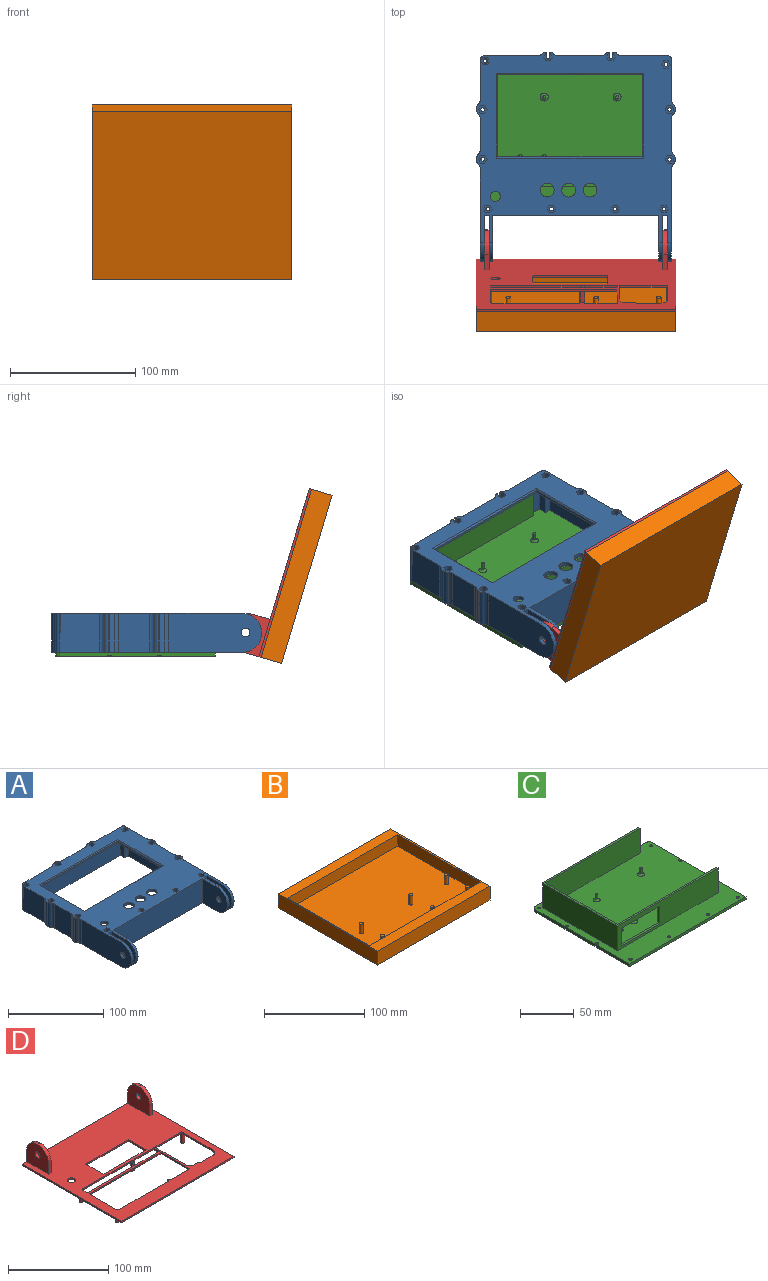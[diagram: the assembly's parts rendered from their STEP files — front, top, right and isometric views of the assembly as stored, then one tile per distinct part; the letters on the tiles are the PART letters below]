
ASSEMBLY  parts=4 mates=3
PART A: 191 faces, bbox 158.4x167x31 mm
  f0: plane 140.4x112mm, normal (0,0,-1), area 7821.9mm2, adj f2,f26,f29,f30,f31,f32,f33,f36
  f1: plane 158.4x152mm, normal (0,0,1), area 11149.3mm2, adj f9,f10,f17,f18,f19,f20,f21,f22
  f2: plane 105x28mm, normal (-1,0,0), area 2939.8mm2, adj f0,f24,f36,f56,f81,f82,f87,f88
  f3: cylinder r=1.5mm len=16mm, axis (0,0,-1), area 150.8mm2, adj f24,f166
  f4: cylinder r=1.5mm len=16mm, axis (0,0,-1), area 150.8mm2, adj f24,f159
  f5: cylinder r=1.5mm len=16mm, axis (0,0,-1), area 150.8mm2, adj f24,f152
  f6: cylinder r=1.5mm len=16mm, axis (0,0,-1), area 150.8mm2, adj f24,f145
  f7: cylinder r=1.5mm len=16mm, axis (0,0,-1), area 110.4mm2, adj f10,f24,f71,f130
  f8: cylinder r=1.5mm len=16mm, axis (0,0,-1), area 110.4mm2, adj f9,f24,f68,f138
  f9: plane 31x3mm, normal (1,0,0), area 62.5mm2, adj f1,f8,f24,f67,f133,f138
  f10: plane 31x3mm, normal (1,0,0), area 62.5mm2, adj f1,f7,f24,f70,f125,f130
  f11: cylinder r=1.5mm len=16mm, axis (0,0,-1), area 150.8mm2, adj f24,f122
  f12: cylinder r=1.75mm len=16mm, axis (0,0,-1), area 175.9mm2, adj f24,f115
  f13: cylinder r=1.5mm len=16mm, axis (0,0,-1), area 150.8mm2, adj f24,f108
  f14: cylinder r=1.5mm len=16mm, axis (0,0,-1), area 150.8mm2, adj f24,f101
  f15: cylinder r=1.5mm len=16mm, axis (0,0,-1), area 150.8mm2, adj f24,f94
  f16: cylinder r=1.5mm len=16mm, axis (0,0,-1), area 150.8mm2, adj f24,f87
  f17: plane 31x24.88mm, normal (1,0,0), area 771.4mm2, adj f1,f24,f175,f178
  f18: plane 73.94x31mm, normal (1,0,0), area 2157.1mm2, adj f1,f24,f43,f44,f45,f62,f177
  f19: plane 31x24.88mm, normal (-1,0,0), area 771.4mm2, adj f1,f24,f179,f182
  f20: plane 31.94x31mm, normal (-1,0,0), area 990.2mm2, adj f1,f24,f51,f181
  f21: plane 34.01x31mm, normal (0,1,0), area 1054.3mm2, adj f1,f24,f187,f190
  f22: plane 36.76x31mm, normal (0,1,0), area 1139.4mm2, adj f1,f24,f50,f189
  f23: plane 42.66x31mm, normal (0,1,0), area 1322.3mm2, adj f1,f24,f51,f188
  f24: plane 158.4x152mm, normal (0,0,-1), area 3979.4mm2, adj f2,f3,f4,f5,f6,f7,f8,f9
  f25: plane 31x4mm, normal (0,-1,0), area 124mm2, adj f1,f24,f42,f58
  f26: plane 135.4x28mm, normal (0,-1,0), area 3791.2mm2, adj f0,f24,f33,f57
  f27: plane 132.4x31mm, normal (0,-1,0), area 4104.4mm2, adj f1,f24,f40,f59
  f28: plane 31x4mm, normal (0,-1,0), area 124mm2, adj f1,f24,f37,f39
  f29: plane 65.5x2mm, normal (1,0,0), area 131mm2, adj f0,f30,f32,f53
  f30: plane 115x2mm, normal (0,-1,0), area 230mm2, adj f0,f29,f31,f52
  f31: plane 65.5x2mm, normal (-1,0,0), area 131mm2, adj f0,f30,f32,f54
  f32: plane 115x2mm, normal (0,1,0), area 230mm2, adj f0,f29,f31,f55
  f33: plane 112x28mm, normal (1,0,0), area 3136mm2, adj f0,f24,f26,f36
  f34: plane 73.94x31mm, normal (-1,0,0), area 2157.1mm2, adj f1,f24,f38,f48,f49,f64,f180
  f35: plane 31.94x31mm, normal (1,0,0), area 990.2mm2, adj f1,f24,f50,f176
  f36: plane 140.4x28mm, normal (0,1,0), area 3931.2mm2, adj f0,f2,f24,f33
  f37: plane 37x31mm, normal (1,0,0), area 1011.9mm2, adj f1,f24,f28,f38,f48,f49,f64
  f38: plane 3x1mm, normal (0,-1,0), area 3mm2, adj f34,f37,f48,f49
  f39: plane 37x31mm, normal (-1,0,0), area 1011.9mm2, adj f1,f24,f28,f41,f46,f47,f63
  f40: plane 37x31mm, normal (1,0,0), area 1011.9mm2, adj f1,f24,f27,f41,f46,f47,f63
  f41: plane 3x1mm, normal (0,-1,0), area 3mm2, adj f39,f40,f46,f47
  f42: plane 37x31mm, normal (-1,0,0), area 1011.9mm2, adj f1,f24,f25,f43,f44,f45,f62
  f43: plane 3x1mm, normal (0,-1,0), area 3mm2, adj f18,f42,f44,f45
  f44: cylinder r=15mm len=15mm, axis (-1,0,0), area 70.7mm2, adj f18,f24,f42,f43
  f45: cylinder r=15mm len=15mm, axis (1,0,0), area 70.7mm2, adj f1,f18,f42,f43
  f46: cylinder r=15mm len=15mm, axis (-1,0,0), area 70.7mm2, adj f24,f39,f40,f41
  f47: cylinder r=15mm len=15mm, axis (1,0,0), area 70.7mm2, adj f1,f39,f40,f41
  f48: cylinder r=15mm len=15mm, axis (1,0,0), area 70.7mm2, adj f1,f34,f37,f38
  f49: cylinder r=15mm len=15mm, axis (-1,0,0), area 70.7mm2, adj f24,f34,f37,f38
  f50: cylinder r=3mm len=31mm, axis (0,0,1), area 146.1mm2, adj f1,f22,f24,f35
  f51: cylinder r=3mm len=31mm, axis (0,0,-1), area 146.1mm2, adj f1,f20,f23,f24
  f52: plane 117x1mm, normal (0,-0.71,0.71), area 164mm2, adj f1,f30,f53,f54
  f53: plane 67.5x1mm, normal (0.71,0,0.71), area 94mm2, adj f1,f29,f52,f55
  f54: plane 67.5x1mm, normal (-0.71,0,0.71), area 94mm2, adj f1,f31,f52,f55
  f55: plane 117x1mm, normal (0,0.71,0.71), area 164mm2, adj f1,f32,f53,f54
  f56: plane 28x5mm, normal (0,-1,0), area 140mm2, adj f0,f2,f24,f57
  f57: plane 28x7mm, normal (-1,0,0), area 196mm2, adj f0,f24,f26,f56
  f58: plane 37x31mm, normal (1,0,0), area 1011.9mm2, adj f1,f24,f25,f60,f61,f65,f66
  f59: plane 37x31mm, normal (-1,0,0), area 1011.9mm2, adj f1,f24,f27,f60,f61,f65,f66
  f60: plane 3x1mm, normal (0,-1,0), area 3mm2, adj f58,f59,f65,f66
  f61: cylinder r=3.5mm len=7mm, axis (-1,0,0), area 66mm2, adj f58,f59
  f62: cylinder r=3.5mm len=7mm, axis (-1,0,0), area 66mm2, adj f18,f42
  f63: cylinder r=3.5mm len=7mm, axis (-1,0,0), area 66mm2, adj f39,f40
  f64: cylinder r=3.5mm len=7mm, axis (-1,0,0), area 66mm2, adj f34,f37
  f65: cylinder r=15mm len=15mm, axis (1,0,0), area 70.7mm2, adj f1,f58,f59,f60
  f66: cylinder r=15mm len=15mm, axis (-1,0,0), area 70.7mm2, adj f24,f58,f59,f60
  f67: plane 31x0.58mm, normal (0,1,0), area 18mm2, adj f1,f9,f24,f186
  f68: plane 31x3mm, normal (-1,0,0), area 62.5mm2, adj f1,f8,f24,f69,f132,f138
  f69: plane 31x1.18mm, normal (0,1,0), area 36.6mm2, adj f1,f24,f68,f185
  f70: plane 31x0.98mm, normal (0,1,0), area 30.4mm2, adj f1,f10,f24,f184
  f71: plane 31x3mm, normal (-1,0,0), area 62.5mm2, adj f1,f7,f24,f72,f124,f130
  f72: plane 31x0.78mm, normal (0,1,0), area 24.2mm2, adj f1,f24,f71,f183
  f73: cylinder r=5.5mm len=11mm, axis (0,0,-1), area 103.7mm2, adj f0,f1
  f74: cylinder r=5.5mm len=11mm, axis (0,0,-1), area 103.7mm2, adj f0,f1
  f75: cylinder r=5.5mm len=11mm, axis (0,0,-1), area 103.7mm2, adj f0,f1
  f76: cylinder r=4mm len=8mm, axis (0,0,-1), area 75.4mm2, adj f0,f1
  f77: plane 31x0.84mm, normal (-1,0,0), area 25.9mm2, adj f1,f24,f171,f172
  f78: plane 31x0.84mm, normal (-1,0,0), area 25.9mm2, adj f1,f24,f173,f174
  f79: plane 31x0.84mm, normal (1,0,0), area 25.9mm2, adj f1,f24,f169,f170
  f80: plane 31x0.84mm, normal (1,0,0), area 25.9mm2, adj f1,f24,f167,f168
  f81: plane 15x3.03mm, normal (0.87,0.5,0), area 52.5mm2, adj f0,f1,f2,f82,f83,f87
  f82: plane 15x3.03mm, normal (0.87,-0.5,0), area 52.5mm2, adj f0,f1,f2,f81,f86,f87
  f83: plane 15x3.5mm, normal (0,1,0), area 52.5mm2, adj f1,f81,f84,f87
  f84: plane 15x3.03mm, normal (-0.87,0.5,0), area 52.5mm2, adj f1,f83,f85,f87
  f85: plane 15x3.03mm, normal (-0.87,-0.5,0), area 52.5mm2, adj f1,f84,f86,f87
  f86: plane 15x3.5mm, normal (0,-1,0), area 52.5mm2, adj f1,f82,f85,f87
  f87: plane 7x6.06mm, normal (0,0,1), area 24.8mm2, adj f2,f16,f81,f82,f83,f84,f85,f86
  f88: plane 15x3.03mm, normal (0.87,0.5,0), area 52.5mm2, adj f0,f1,f2,f89,f90,f94
  f89: plane 15x3.03mm, normal (0.87,-0.5,0), area 52.5mm2, adj f0,f1,f2,f88,f93,f94
  f90: plane 15x3.5mm, normal (0,1,0), area 52.5mm2, adj f1,f88,f91,f94
  f91: plane 15x3.03mm, normal (-0.87,0.5,0), area 52.5mm2, adj f1,f90,f92,f94
  f92: plane 15x3.03mm, normal (-0.87,-0.5,0), area 52.5mm2, adj f1,f91,f93,f94
  f93: plane 15x3.5mm, normal (0,-1,0), area 52.5mm2, adj f1,f89,f92,f94
  f94: plane 7x6.06mm, normal (0,0,1), area 24.8mm2, adj f2,f15,f88,f89,f90,f91,f92,f93
  f95: plane 15x3.03mm, normal (0.87,0.5,0), area 52.5mm2, adj f1,f96,f100,f101
  f96: plane 15x3.5mm, normal (0,1,0), area 52.5mm2, adj f1,f95,f97,f101
  f97: plane 15x3.03mm, normal (-0.87,0.5,0), area 52.5mm2, adj f1,f96,f98,f101
  f98: plane 15x3.03mm, normal (-0.87,-0.5,0), area 52.5mm2, adj f1,f97,f99,f101
  f99: plane 15x3.5mm, normal (0,-1,0), area 52.5mm2, adj f1,f98,f100,f101
  f100: plane 15x3.03mm, normal (0.87,-0.5,0), area 52.5mm2, adj f1,f95,f99,f101
  f101: plane 7x6.06mm, normal (0,0,1), area 24.8mm2, adj f14,f95,f96,f97,f98,f99,f100
  f102: plane 15x3.03mm, normal (0.87,0.5,0), area 52.5mm2, adj f1,f103,f107,f108
  f103: plane 15x3.5mm, normal (0,1,0), area 52.5mm2, adj f1,f102,f104,f108
  f104: plane 15x3.03mm, normal (-0.87,0.5,0), area 52.5mm2, adj f1,f103,f105,f108
  f105: plane 15x3.03mm, normal (-0.87,-0.5,0), area 52.5mm2, adj f1,f104,f106,f108
  f106: plane 15x3.5mm, normal (0,-1,0), area 52.5mm2, adj f1,f105,f107,f108
  f107: plane 15x3.03mm, normal (0.87,-0.5,0), area 52.5mm2, adj f1,f102,f106,f108
  f108: plane 7x6.06mm, normal (0,0,1), area 24.8mm2, adj f13,f102,f103,f104,f105,f106,f107
  f109: plane 15x3.03mm, normal (0.87,0.5,0), area 52.5mm2, adj f1,f110,f114,f115
  f110: plane 15x3.5mm, normal (0,1,0), area 52.5mm2, adj f1,f109,f111,f115
  f111: plane 15x3.03mm, normal (-0.87,0.5,0), area 52.5mm2, adj f1,f110,f112,f115
  f112: plane 15x3.03mm, normal (-0.87,-0.5,0), area 52.5mm2, adj f1,f111,f113,f115
  f113: plane 15x3.5mm, normal (0,-1,0), area 52.5mm2, adj f1,f112,f114,f115
  f114: plane 15x3.03mm, normal (0.87,-0.5,0), area 52.5mm2, adj f1,f109,f113,f115
  f115: plane 7x6.06mm, normal (0,0,1), area 22.2mm2, adj f12,f109,f110,f111,f112,f113,f114
  f116: plane 15x3.03mm, normal (0.87,0.5,0), area 52.5mm2, adj f1,f117,f121,f122
  f117: plane 15x3.5mm, normal (0,1,0), area 52.5mm2, adj f1,f116,f118,f122
  f118: plane 15x3.03mm, normal (-0.87,0.5,0), area 52.5mm2, adj f1,f117,f119,f122
  f119: plane 15x3.03mm, normal (-0.87,-0.5,0), area 52.5mm2, adj f1,f118,f120,f122
  f120: plane 15x3.5mm, normal (0,-1,0), area 52.5mm2, adj f1,f119,f121,f122
  f121: plane 15x3.03mm, normal (0.87,-0.5,0), area 52.5mm2, adj f1,f116,f120,f122
  f122: plane 7x6.06mm, normal (0,0,1), area 24.8mm2, adj f11,f116,f117,f118,f119,f120,f121
  f123: plane 15x3.03mm, normal (-0.87,-0.5,0), area 52.5mm2, adj f1,f124,f129,f130
  f124: plane 15x0.63mm, normal (0,-1,0), area 9.5mm2, adj f1,f71,f123,f130
  f125: plane 15x0.63mm, normal (0,-1,0), area 9.5mm2, adj f1,f10,f126,f130
  f126: plane 15x3.03mm, normal (0.87,-0.5,0), area 52.5mm2, adj f1,f125,f127,f130
  f127: plane 15x3.03mm, normal (0.87,0.5,0), area 52.5mm2, adj f1,f126,f128,f130
  f128: plane 15x3.5mm, normal (0,1,0), area 52.5mm2, adj f1,f127,f129,f130
  f129: plane 15x3.03mm, normal (-0.87,0.5,0), area 52.5mm2, adj f1,f123,f128,f130
  f130: plane 7x6.06mm, normal (0,0,1), area 21mm2, adj f7,f10,f71,f123,f124,f125,f126,f127
  f131: plane 15x3.03mm, normal (-0.87,-0.5,0), area 52.5mm2, adj f1,f132,f137,f138
  f132: plane 15x0.63mm, normal (0,-1,0), area 9.5mm2, adj f1,f68,f131,f138
  f133: plane 15x0.63mm, normal (0,-1,0), area 9.5mm2, adj f1,f9,f134,f138
  f134: plane 15x3.03mm, normal (0.87,-0.5,0), area 52.5mm2, adj f1,f133,f135,f138
  f135: plane 15x3.03mm, normal (0.87,0.5,0), area 52.5mm2, adj f1,f134,f136,f138
  f136: plane 15x3.5mm, normal (0,1,0), area 52.5mm2, adj f1,f135,f137,f138
  f137: plane 15x3.03mm, normal (-0.87,0.5,0), area 52.5mm2, adj f1,f131,f136,f138
  f138: plane 7x6.06mm, normal (0,0,1), area 21mm2, adj f8,f9,f68,f131,f132,f133,f134,f135
  f139: plane 15x3.03mm, normal (0.87,0.5,0), area 52.5mm2, adj f1,f140,f144,f145
  f140: plane 15x3.5mm, normal (0,1,0), area 52.5mm2, adj f1,f139,f141,f145
  f141: plane 15x3.03mm, normal (-0.87,0.5,0), area 52.5mm2, adj f1,f140,f142,f145
  f142: plane 15x3.03mm, normal (-0.87,-0.5,0), area 52.5mm2, adj f1,f141,f143,f145
  f143: plane 15x3.5mm, normal (0,-1,0), area 52.5mm2, adj f1,f142,f144,f145
  f144: plane 15x3.03mm, normal (0.87,-0.5,0), area 52.5mm2, adj f1,f139,f143,f145
  f145: plane 7x6.06mm, normal (0,0,1), area 24.8mm2, adj f6,f139,f140,f141,f142,f143,f144
  f146: plane 15x3.03mm, normal (0.87,0.5,0), area 52.5mm2, adj f1,f147,f151,f152
  f147: plane 15x3.5mm, normal (0,1,0), area 52.5mm2, adj f1,f146,f148,f152
  f148: plane 15x3.03mm, normal (-0.87,0.5,0), area 52.5mm2, adj f1,f147,f149,f152
  f149: plane 15x3.03mm, normal (-0.87,-0.5,0), area 52.5mm2, adj f1,f148,f150,f152
  f150: plane 15x3.5mm, normal (0,-1,0), area 52.5mm2, adj f1,f149,f151,f152
  f151: plane 15x3.03mm, normal (0.87,-0.5,0), area 52.5mm2, adj f1,f146,f150,f152
  f152: plane 7x6.06mm, normal (0,0,1), area 24.8mm2, adj f5,f146,f147,f148,f149,f150,f151
  f153: plane 15x3.03mm, normal (0.87,0.5,0), area 52.5mm2, adj f1,f154,f158,f159
  f154: plane 15x3.5mm, normal (0,1,0), area 52.5mm2, adj f1,f153,f155,f159
  f155: plane 15x3.03mm, normal (-0.87,0.5,0), area 52.5mm2, adj f1,f154,f156,f159
  f156: plane 15x3.03mm, normal (-0.87,-0.5,0), area 52.5mm2, adj f1,f155,f157,f159
  f157: plane 15x3.5mm, normal (0,-1,0), area 52.5mm2, adj f1,f156,f158,f159
  f158: plane 15x3.03mm, normal (0.87,-0.5,0), area 52.5mm2, adj f1,f153,f157,f159
  f159: plane 7x6.06mm, normal (0,0,1), area 24.8mm2, adj f4,f153,f154,f155,f156,f157,f158
  f160: plane 15x3.03mm, normal (0.87,0.5,0), area 52.5mm2, adj f1,f161,f165,f166
  f161: plane 15x3.5mm, normal (0,1,0), area 52.5mm2, adj f1,f160,f162,f166
  f162: plane 15x3.03mm, normal (-0.87,0.5,0), area 52.5mm2, adj f1,f161,f163,f166
  f163: plane 15x3.03mm, normal (-0.87,-0.5,0), area 52.5mm2, adj f1,f162,f164,f166
  f164: plane 15x3.5mm, normal (0,-1,0), area 52.5mm2, adj f1,f163,f165,f166
  f165: plane 15x3.03mm, normal (0.87,-0.5,0), area 52.5mm2, adj f1,f160,f164,f166
  f166: plane 7x6.06mm, normal (0,0,1), area 24.8mm2, adj f3,f160,f161,f162,f163,f164,f165
  f167: cylinder r=5mm len=31mm, axis (0,0,1), area 123.3mm2, adj f1,f24,f80,f175
  f168: cylinder r=5mm len=31mm, axis (0,0,1), area 123.3mm2, adj f1,f24,f80,f176
  f169: cylinder r=5mm len=31mm, axis (0,0,1), area 123.3mm2, adj f1,f24,f79,f177
  f170: cylinder r=5mm len=31mm, axis (0,0,1), area 123.3mm2, adj f1,f24,f79,f178
  f171: cylinder r=5mm len=31mm, axis (0,0,-1), area 123.3mm2, adj f1,f24,f77,f179
  f172: cylinder r=5mm len=31mm, axis (0,0,-1), area 123.3mm2, adj f1,f24,f77,f180
  f173: cylinder r=5mm len=31mm, axis (0,0,-1), area 123.3mm2, adj f1,f24,f78,f181
  f174: cylinder r=5mm len=31mm, axis (0,0,-1), area 123.3mm2, adj f1,f24,f78,f182
  f175: cylinder r=5mm len=31mm, axis (0,0,1), area 123.3mm2, adj f1,f17,f24,f167
  f176: cylinder r=5mm len=31mm, axis (0,0,1), area 123.3mm2, adj f1,f24,f35,f168
  f177: cylinder r=5mm len=31mm, axis (0,0,1), area 123.3mm2, adj f1,f18,f24,f169
  f178: cylinder r=5mm len=31mm, axis (0,0,1), area 123.3mm2, adj f1,f17,f24,f170
  f179: cylinder r=5mm len=31mm, axis (0,0,-1), area 123.3mm2, adj f1,f19,f24,f171
  f180: cylinder r=5mm len=31mm, axis (0,0,-1), area 123.3mm2, adj f1,f24,f34,f172
  f181: cylinder r=5mm len=31mm, axis (0,0,-1), area 123.3mm2, adj f1,f20,f24,f173
  f182: cylinder r=5mm len=31mm, axis (0,0,-1), area 123.3mm2, adj f1,f19,f24,f174
  f183: cylinder r=3mm len=31mm, axis (0,0,1), area 83.3mm2, adj f1,f24,f72,f187
  f184: cylinder r=3mm len=31mm, axis (0,0,-1), area 83.3mm2, adj f1,f24,f70,f188
  f185: cylinder r=3mm len=31mm, axis (0,0,1), area 83.3mm2, adj f1,f24,f69,f189
  f186: cylinder r=3mm len=31mm, axis (0,0,-1), area 83.3mm2, adj f1,f24,f67,f190
  f187: cylinder r=5mm len=31mm, axis (0,0,1), area 138.8mm2, adj f1,f21,f24,f183
  f188: cylinder r=5mm len=31mm, axis (0,0,-1), area 138.8mm2, adj f1,f23,f24,f184
  f189: cylinder r=5mm len=31mm, axis (0,0,1), area 138.8mm2, adj f1,f22,f24,f185
  f190: cylinder r=5mm len=31mm, axis (0,0,-1), area 138.8mm2, adj f1,f21,f24,f186
PART B: 23 faces, bbox 159x140x17 mm
  f0: plane 155.5x116mm, normal (0,0,1), area 17962.6mm2, adj f2,f3,f4,f5,f11,f13,f15,f17
  f1: plane 159x140mm, normal (0,0,-1), area 22260mm2, adj f6,f7,f8,f9
  f2: plane 155.5x14mm, normal (0,-1,0), area 2177mm2, adj f0,f3,f5,f10
  f3: plane 116x14mm, normal (1,0,0), area 1624mm2, adj f0,f2,f4,f10
  f4: plane 155.5x14mm, normal (0,1,0), area 2177mm2, adj f0,f3,f5,f10
  f5: plane 116x14mm, normal (-1,0,0), area 1624mm2, adj f0,f2,f4,f10
  f6: plane 159x17mm, normal (0,1,0), area 2703mm2, adj f1,f7,f9,f10
  f7: plane 140x17mm, normal (-1,0,0), area 2380mm2, adj f1,f6,f8,f10
  f8: plane 159x17mm, normal (0,-1,0), area 2703mm2, adj f1,f7,f9,f10
  f9: plane 140x17mm, normal (1,0,0), area 2380mm2, adj f1,f6,f8,f10
  f10: plane 159x140mm, normal (0,0,1), area 4222mm2, adj f2,f3,f4,f5,f6,f7,f8,f9
  f11: cylinder r=2mm len=11.4mm, axis (0,0,-1), area 143.3mm2, adj f0,f12
  f12: plane 4x4mm, normal (0,0,1), area 12.6mm2, adj f11
  f13: cylinder r=2mm len=11.4mm, axis (0,0,-1), area 143.3mm2, adj f0,f14
  f14: plane 4x4mm, normal (0,0,1), area 12.6mm2, adj f13
  f15: cylinder r=2mm len=11.4mm, axis (0,0,-1), area 143.3mm2, adj f0,f16
  f16: plane 4x4mm, normal (0,0,1), area 12.6mm2, adj f15
  f17: cylinder r=2mm len=11.4mm, axis (0,0,-1), area 143.3mm2, adj f0,f18
  f18: plane 4x4mm, normal (0,0,1), area 12.6mm2, adj f17
  f19: cylinder r=2mm len=11.4mm, axis (0,0,-1), area 143.3mm2, adj f0,f20
  f20: plane 4x4mm, normal (0,0,1), area 12.6mm2, adj f19
  f21: cylinder r=2mm len=11.4mm, axis (0,0,-1), area 143.3mm2, adj f0,f22
  f22: plane 4x4mm, normal (0,0,1), area 12.6mm2, adj f21
PART C: 71 faces, bbox 152.4x127x31 mm
  f0: plane 124x3mm, normal (1,0,0), area 366.3mm2, adj f17,f18,f19,f44,f63,f64,f65,f66
  f1: cylinder r=1.5mm len=3mm, axis (0,0,-1), area 18.8mm2, adj f18,f66
  f2: cylinder r=1.5mm len=3mm, axis (0,0,-1), area 18.8mm2, adj f18,f64
  f3: cylinder r=1.5mm len=3mm, axis (0,0,-1), area 18.8mm2, adj f18,f62
  f4: cylinder r=1.5mm len=3mm, axis (0,0,-1), area 18.8mm2, adj f18,f60
  f5: cylinder r=1.5mm len=3mm, axis (0,0,-1), area 18.8mm2, adj f18,f58
  f6: cylinder r=1.5mm len=3mm, axis (0,0,-1), area 18.8mm2, adj f18,f56
  f7: cylinder r=1.5mm len=3mm, axis (0,0,-1), area 18.8mm2, adj f18,f54
  f8: cylinder r=1.5mm len=3mm, axis (0,0,-1), area 18.8mm2, adj f18,f52
  f9: cylinder r=1.5mm len=3mm, axis (0,0,-1), area 18.8mm2, adj f18,f50
  f10: cylinder r=1.5mm len=3mm, axis (0,0,-1), area 18.8mm2, adj f18,f48
  f11: plane 44.18x3mm, normal (0,1,0), area 131.6mm2, adj f18,f19,f44,f46,f69,f70
  f12: plane 47.86x3mm, normal (0,1,0), area 141.8mm2, adj f18,f19,f45,f46,f67,f68,f69,f70
  f13: plane 129.94x28mm, normal (0,1,0), area 2638.4mm2, adj f18,f20,f22,f26,f35,f36,f37,f38
  f14: plane 131.94x28mm, normal (0,-1,0), area 2694.4mm2, adj f18,f20,f22,f23,f35,f36,f37,f38
  f15: plane 49.88x3mm, normal (0,1,0), area 148.7mm2, adj f18,f19,f43,f45,f67,f68
  f16: plane 124x3mm, normal (-1,0,0), area 367.9mm2, adj f17,f18,f19,f43,f49,f50,f51,f52
  f17: plane 152.4x3mm, normal (0,-1,0), area 457.2mm2, adj f0,f16,f18,f19
  f18: plane 152.4x127mm, normal (0,0,1), area 18439.1mm2, adj f0,f1,f2,f3,f4,f5,f6,f7
  f19: plane 152.4x127mm, normal (0,0,-1), area 19169.9mm2, adj f0,f11,f12,f15,f16,f17,f43,f44
  f20: plane 131.94x98mm, normal (0,0,1), area 703.9mm2, adj f13,f14,f21,f22,f23,f24,f25,f26
  f21: plane 124x28mm, normal (0,-1,0), area 3472mm2, adj f18,f20,f25,f26
  f22: plane 28x2mm, normal (1,0,0), area 56mm2, adj f13,f14,f18,f20
  f23: plane 98x28mm, normal (-1,0,0), area 2744mm2, adj f14,f18,f20,f24
  f24: plane 126x28mm, normal (0,1,0), area 3528mm2, adj f18,f20,f23,f25
  f25: plane 28x2mm, normal (1,0,0), area 56mm2, adj f18,f20,f21,f24
  f26: plane 94x28mm, normal (1,0,0), area 2632mm2, adj f13,f18,f20,f21
  f27: cylinder r=1.15mm len=5mm, axis (0,0,-1), area 36.1mm2, adj f28,f39
  f28: plane 2.3x2.3mm, normal (0,0,1), area 4.2mm2, adj f27
  f29: cylinder r=1.15mm len=5mm, axis (0,0,-1), area 36.1mm2, adj f30,f40
  f30: plane 2.3x2.3mm, normal (0,0,1), area 4.2mm2, adj f29
  f31: cylinder r=1.15mm len=5mm, axis (0,0,-1), area 36.1mm2, adj f32,f41
  f32: plane 2.3x2.3mm, normal (0,0,1), area 4.2mm2, adj f31
  f33: cylinder r=1.15mm len=5mm, axis (0,0,-1), area 36.1mm2, adj f34,f42
  f34: plane 2.3x2.3mm, normal (0,0,1), area 4.2mm2, adj f33
  f35: plane 50x2mm, normal (0,0,-1), area 100mm2, adj f13,f14,f36,f38
  f36: plane 20x2mm, normal (1,0,0), area 40mm2, adj f13,f14,f35,f37
  f37: plane 50x2mm, normal (0,0,1), area 100mm2, adj f13,f14,f36,f38
  f38: plane 20x2mm, normal (-1,0,0), area 40mm2, adj f13,f14,f35,f37
  f39: torus R=3.15mm, axis (0,0,1), area 37mm2, adj f18,f27
  f40: torus R=3.15mm, axis (0,0,1), area 37mm2, adj f18,f29
  f41: torus R=3.15mm, axis (0,0,1), area 37mm2, adj f18,f31
  f42: torus R=3.15mm, axis (0,0,1), area 37mm2, adj f18,f33
  f43: cylinder r=3mm len=3mm, axis (0,0,1), area 14.1mm2, adj f15,f16,f18,f19
  f44: cylinder r=3mm len=3mm, axis (0,0,-1), area 14.1mm2, adj f0,f11,f18,f19
  f45: cylinder r=1.5mm len=3mm, axis (0,0,-1), area 13.8mm2, adj f12,f15,f18,f68
  f46: cylinder r=1.5mm len=3mm, axis (0,0,-1), area 13.8mm2, adj f11,f12,f18,f70
  f47: cylinder r=2.25mm len=4.5mm, axis (0,0,-1), area 14.1mm2, adj f19,f48
  f48: plane 4.5x4.5mm, normal (0,0,-1), area 8.8mm2, adj f10,f47
  f49: cylinder r=2.25mm len=4.5mm, axis (0,0,-1), area 12mm2, adj f16,f19,f50
  f50: plane 4.5x4.25mm, normal (0,0,-1), area 8.5mm2, adj f9,f16,f49
  f51: cylinder r=2.25mm len=4.5mm, axis (0,0,-1), area 12mm2, adj f16,f19,f52
  f52: plane 4.5x4.25mm, normal (0,0,-1), area 8.5mm2, adj f8,f16,f51
  f53: cylinder r=2.25mm len=4.5mm, axis (0,0,-1), area 14.1mm2, adj f19,f54
  f54: plane 4.5x4.5mm, normal (0,0,-1), area 8.8mm2, adj f7,f53
  f55: cylinder r=2.25mm len=4.5mm, axis (0,0,-1), area 14.1mm2, adj f19,f56
  f56: plane 4.5x4.5mm, normal (0,0,-1), area 8.8mm2, adj f6,f55
  f57: cylinder r=2.25mm len=4.5mm, axis (0,0,-1), area 14.1mm2, adj f19,f58
  f58: plane 4.5x4.5mm, normal (0,0,-1), area 8.8mm2, adj f5,f57
  f59: cylinder r=2.25mm len=4.5mm, axis (0,0,-1), area 14.1mm2, adj f19,f60
  f60: plane 4.5x4.5mm, normal (0,0,-1), area 8.8mm2, adj f4,f59
  f61: cylinder r=2.25mm len=4.5mm, axis (0,0,-1), area 14.1mm2, adj f19,f62
  f62: plane 4.5x4.5mm, normal (0,0,-1), area 8.8mm2, adj f3,f61
  f63: cylinder r=2.25mm len=4.5mm, axis (0,0,-1), area 11.1mm2, adj f0,f19,f64
  f64: plane 4.5x4mm, normal (0,0,-1), area 7.9mm2, adj f0,f2,f63
  f65: cylinder r=2.25mm len=4.5mm, axis (0,0,-1), area 11.1mm2, adj f0,f19,f66
  f66: plane 4.5x4mm, normal (0,0,-1), area 7.9mm2, adj f0,f1,f65
  f67: cylinder r=2.25mm len=4.5mm, axis (0,0,-1), area 9.1mm2, adj f12,f15,f19,f68
  f68: plane 4.5x3.25mm, normal (0,0,-1), area 6mm2, adj f12,f15,f45,f67
  f69: cylinder r=2.25mm len=4.5mm, axis (0,0,-1), area 9.1mm2, adj f11,f12,f19,f70
  f70: plane 4.5x3.25mm, normal (0,0,-1), area 6mm2, adj f11,f12,f46,f69
PART D: 57 faces, bbox 159x140x42.5 mm
  f0: plane 159x140mm, normal (0,0,-1), area 13876.5mm2, adj f3,f4,f5,f6,f22,f23,f24,f25
  f1: plane 159x140mm, normal (0,0,1), area 13703.8mm2, adj f3,f4,f5,f6,f7,f8,f9,f11
  f2: plane 3.46x1mm, normal (0,0,-1), area 2.5mm2, adj f21,f49
  f3: plane 159x15.3mm, normal (0,1,0), area 388.8mm2, adj f0,f1,f4,f6,f8,f9,f12,f13
  f4: plane 140x1.8mm, normal (-1,0,0), area 252mm2, adj f0,f1,f3,f5
  f5: plane 159x1.8mm, normal (0,-1,0), area 286.2mm2, adj f0,f1,f4,f6
  f6: plane 140x1.8mm, normal (1,0,0), area 252mm2, adj f0,f1,f3,f5
  f7: plane 13.5x3.8mm, normal (0,-1,0), area 51.3mm2, adj f1,f8,f9,f16
  f8: plane 31x28.5mm, normal (1,0,0), area 748.4mm2, adj f1,f3,f7,f10,f15,f16,f20
  f9: plane 31x28.5mm, normal (-1,0,0), area 748.4mm2, adj f1,f3,f7,f10,f15,f16,f20
  f10: plane 3.8x1mm, normal (0,0,1), area 3.8mm2, adj f8,f9,f15,f16
  f11: plane 13.5x3.8mm, normal (0,-1,0), area 51.3mm2, adj f1,f12,f13,f18
  f12: plane 31x28.5mm, normal (1,0,0), area 748.4mm2, adj f1,f3,f11,f14,f17,f18,f19
  f13: plane 31x28.5mm, normal (-1,0,0), area 748.4mm2, adj f1,f3,f11,f14,f17,f18,f19
  f14: plane 3.8x1mm, normal (0,0,1), area 3.8mm2, adj f12,f13,f17,f18
  f15: cylinder r=15mm len=15mm, axis (1,0,0), area 89.5mm2, adj f3,f8,f9,f10
  f16: cylinder r=15mm len=15mm, axis (-1,0,0), area 89.5mm2, adj f7,f8,f9,f10
  f17: cylinder r=15mm len=15mm, axis (1,0,0), area 89.5mm2, adj f3,f12,f13,f14
  f18: cylinder r=15mm len=15mm, axis (-1,0,0), area 89.5mm2, adj f11,f12,f13,f14
  f19: cylinder r=3.5mm len=7mm, axis (1,0,0), area 83.6mm2, adj f12,f13
  f20: cylinder r=3.5mm len=7mm, axis (1,0,0), area 83.6mm2, adj f8,f9
  f21: cylinder r=2mm len=3.46mm, axis (0,0,1), area 7.5mm2, adj f1,f2,f22,f27
  f22: plane 70.52x1.8mm, normal (0,-1,0), area 126.9mm2, adj f0,f1,f21,f23
  f23: cylinder r=2mm len=14mm, axis (0,0,1), area 157.6mm2, adj f0,f1,f22,f24,f52
  f24: plane 6.14x1.8mm, normal (1,0,0), area 11.1mm2, adj f0,f1,f23,f25
  f25: plane 101.5x1.8mm, normal (0,1,0), area 182.7mm2, adj f0,f1,f24,f26
  f26: plane 8x1.8mm, normal (-1,0,0), area 14.4mm2, adj f0,f1,f25,f27
  f27: plane 26.27x1.8mm, normal (0,-1,0), area 47.3mm2, adj f0,f1,f21,f26
  f28: plane 25x1.8mm, normal (1,0,0), area 45mm2, adj f0,f1,f29,f31
  f29: plane 60x1.8mm, normal (0,1,0), area 108mm2, adj f0,f1,f28,f30
  f30: plane 25x1.8mm, normal (-1,0,0), area 45mm2, adj f0,f1,f29,f31
  f31: plane 60x1.8mm, normal (0,-1,0), area 108mm2, adj f0,f1,f28,f30
  f32: plane 16.56x1.8mm, normal (0,1,0), area 29.8mm2, adj f0,f1,f33,f40
  f33: cylinder r=8mm len=8mm, axis (0,0,1), area 22.6mm2, adj f0,f1,f32,f34
  f34: plane 43x1.8mm, normal (-1,0,0), area 77.4mm2, adj f0,f1,f33,f35
  f35: plane 37.56x1.8mm, normal (0,-1,0), area 67.6mm2, adj f0,f1,f34,f36
  f36: plane 44x1.8mm, normal (1,0,0), area 79.2mm2, adj f0,f1,f35,f37
  f37: cylinder r=5mm len=5mm, axis (0,0,1), area 14.1mm2, adj f0,f1,f36,f38
  f38: plane 6.5x1.8mm, normal (0,1,0), area 11.7mm2, adj f0,f1,f37,f39
  f39: cylinder r=1.5mm len=1.8mm, axis (0,0,1), area 4.2mm2, adj f0,f1,f38,f40
  f40: plane 1.8x0.5mm, normal (1,0,0), area 0.9mm2, adj f0,f1,f32,f39
  f41: cylinder r=4mm len=8mm, axis (0,0,1), area 45.2mm2, adj f0,f1
  f42: plane 37.96x1.8mm, normal (1,0,0), area 68.3mm2, adj f0,f1,f43,f48
  f43: cylinder r=2mm len=14mm, axis (0,0,1), area 159mm2, adj f0,f1,f42,f44,f53
  f44: plane 70.05x1.8mm, normal (0,1,0), area 126.1mm2, adj f0,f1,f43,f45
  f45: cylinder r=2mm len=14mm, axis (0,0,1), area 164.6mm2, adj f0,f1,f44,f46,f54
  f46: plane 26x1.8mm, normal (0,1,0), area 46.8mm2, adj f0,f1,f45,f47
  f47: plane 40.4x1.8mm, normal (-1,0,0), area 72.7mm2, adj f0,f1,f46,f48
  f48: plane 101.5x1.8mm, normal (0,-1,0), area 182.7mm2, adj f0,f1,f42,f47
  f49: plane 12.2x3.46mm, normal (0,-1,0), area 42.3mm2, adj f2,f50,f51
  f50: cylinder r=2mm len=12.2mm, axis (0,0,1), area 102.2mm2, adj f0,f49,f51
  f51: plane 4x3mm, normal (0,0,-1), area 10.1mm2, adj f49,f50
  f52: plane 4x4mm, normal (0,0,-1), area 12.6mm2, adj f23
  f53: plane 4x4mm, normal (0,0,-1), area 12.6mm2, adj f43
  f54: plane 4x4mm, normal (0,0,-1), area 12.6mm2, adj f45
  f55: cylinder r=2mm len=12.2mm, axis (0,0,1), area 153.3mm2, adj f0,f56
  f56: plane 4x4mm, normal (0,0,-1), area 12.6mm2, adj f55
PLACE A t=(1,-1,8)mm fixed
PLACE B rot(axis=(-1,0,0),73.3deg) t=(-4.4,-56.35,-236)mm
PLACE C t=(1,-1,-26.18)mm
PLACE D rot(axis=(-1,0,0),73.3deg) t=(-3.4,-79.68,-98.93)mm
MATE revolute D.f19 <-> A.f61  axis (1,0,0) through (-68.2,-88.8,-7.19)mm
MATE fastened B.f10 <-> D.f0  axis (0,0.96,0.29) through (80.6,-141.4,107.02)mm
MATE slider C.f44 <-> A.f50  axis (0,0,1) through (74.2,59.5,-23.18)mm
